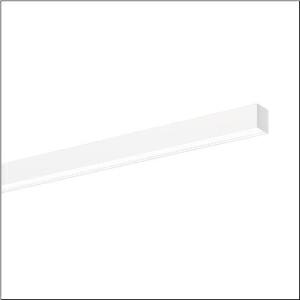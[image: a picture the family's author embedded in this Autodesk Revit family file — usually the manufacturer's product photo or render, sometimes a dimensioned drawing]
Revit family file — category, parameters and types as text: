
# Revit family: silica_r__21_51mx20tct5w_c7ea
name_source: partatom
category: Lighting Fixtures
units: mm (PartAtom-declared; Revit-internal decimal feet)

## family parameters
Cut with Voids When Loaded = No
Host = Face
Light Source = No
Part Type = Normal
Room Calculation Point = No
Round Connector Dimension = Use Diameter
Shared = No

## types (1)
- --- (1 x LED, 6000 lm, 51.3 W, 6500K)
    Apparent Load = 51 VA
    CIE Flux Codes = 48 79 96 100 100
    Color Rendering = 80
    Color Temperature = 6500K
    Default Elevation = 1800 mm
    Description = Silica® 21, office luminaire, primary optical cover: cover, of PMMA, opal, light emission: direct distribution, primary light characteristic: symmetric, installation type: surface-mounted, LED, rated luminous flux: 6.000lm, luminous efficacy: 112lm/W, light colour: 8tw, colour temperature: 2700..6500K, control gear: ECG DALI, with terminal, 3+2-pole, max. 2.5mm², mains connection: 220..240V, AC, 50/60Hz, rated input power: 53.8W, luminaire housing, of aluminium, traffic white (RAL 9016), length: 3.004mm, width: 53mm, height: 53mm, protection rating (complete): IP20, insulation class (complete): insulation class I (protective earthing), certification: CE, permissible operating ambient temperature: 0..+35°C, standard: EN 50419, packaging unit: 1 piece
    Height = 0 mm  [stored 0 ft]
    Lamp = 1 x LED
    Lamp Light Flux = 6000 lm
    Lamp Power = 51.3 W
    Lamp count = 1
    Length = 3004 mm
    Luminous efficacy = 117 lm/W
    Manufacturer = Siteco
    ModVariant = No
    Model = 51MX20TCT5W
    Mounting Place = Ceiling
    Mounting Type = Recessed
    Number of Poles = 1
    OnlyDefault = Yes
    Power Factor = 1
    Product Name = Silica® 21
    Product group = office luminaire | ceiling recessed
    ProductGroupID = 401
    Protection Class = Protection class I
    Protection Degree = IP 20
    RLX_Detail_Level = 1
    RLX_Emergency_Light_Flux = 0 lm
    RLX_Emergency_Type = 0
    RLX_Emergency_Type_DB = No
    RlxData = <blob elided: 20689 chars, md5=1cb802c1>
    Socket = socket
    Standby Power = 0 W
    System Light Flux = 6000 lm
    System Power = 51 W
    Type Comments = individual setting
    Type Image = l_1297777.jpg
    URL = http://relux.com
    VarID = @adj_071023
    Voltage = 0 V
    Weight = 0.00 kg
    Width = 53 mm

note: [stored X ft] marks values corroborated as IEEE doubles in the binary element streams (Revit-internal decimal feet)

## geometry (parser evidence)
native form markers: Blend x4, Sweep x11
no freeform markers — native parametric forms only
